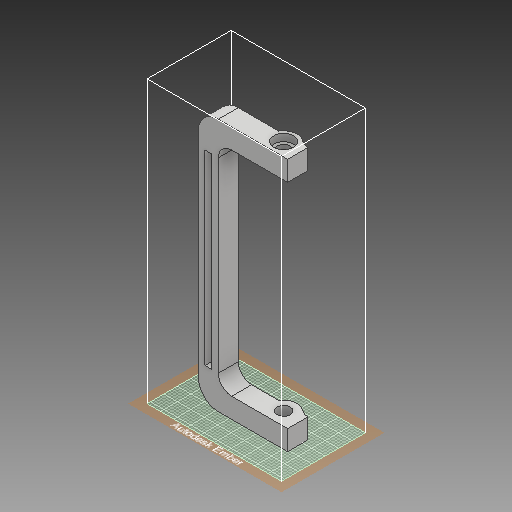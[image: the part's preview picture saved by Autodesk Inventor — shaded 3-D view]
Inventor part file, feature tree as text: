
AUTODESK INVENTOR PART (.ipt)
format: ipt  version: 2018 (Build 220112000, 112)  size: 412,160 bytes
history: native  units: in
note: dims shown in document units (in); Inventor stores cm internally (conversion verified against a paired STEP export)
features: sketch x21, extrude x14, fillet x6, hole x2, plane x1, mirror x1
ambient origin geometry x8: Origin, YZ Plane, XZ Plane, XY Plane, X Axis, Y Axis, Z Axis, Center Point
bodies: Solid1 (feature_tree)
feature tree (45):
  extrude  "Extrusion1"  Depth=0.375in
  sketch  "Sketch2"  dims[d3=0.375in d4=0.5in d5=0.375in d6=0.0in]
  extrude  "Extrusion2"  Depth=0.375in
  fillet  "Fillet1"  Radius=0.375in
  extrude  "Extrusion3"  Depth=0.375in
  extrude  "Extrusion4"  Depth=0.25in
  plane  "Work Plane1"
  mirror  "Mirror1"
  fillet  "Fillet2"  Radius=0.24in
  extrude  "Extrusion5"  Depth=0.375in
  sketch  "Sketch6"  dims[d17=1.0in d18=0.0in d19=0.24in d20=0.0in]
  extrude  "Extrusion6"  Depth=0.24in TaperAngle=0.0deg
  extrude  "Extrusion7"  Depth=0.375in
  fillet  "Fillet3"  Radius=0.25in
  fillet  "Fillet4"  Radius=0.375in
  fillet  "Fillet5"  Radius=0.25in
  fillet  "Fillet6"  Radius=0.125in
  sketch  "Sketch9"  dims[d30=0.125in d31=0.125in]
  extrude  "Extrusion8"  Depth=0.035in
  sketch  "Sketch11"  dims[d35=0.2in]
  sketch  "Sketch12"  dims[d36=0.2in d37=0.75in d38=0.375in d39=0.25in d40=0.5635in d41=0.35in d42=0.0in]
  hole  "Hole1"  [1 undecoded]
  hole  "Hole2"  [1 undecoded]
  sketch  "Sketch14"  dims[d51=3.5in d52=0.375in d53=0.0in]
  extrude  "Extrusion9"  Depth=0.375in
  extrude  "Extrusion10"  Depth=0.375in TaperAngle=0.0deg
  sketch  "Sketch17"  dims[d60=0.4375in d61=0.0in d62=0.39in]
  extrude  "Extrusion11"  Depth=0.26in
  extrude  "Extrusion12"  Depth=0.26in
  extrude  "Extrusion13"  Depth=0.39in
  extrude  "Extrusion14"  Depth=0.39in
  sketch  "Sketch1"  dims[d0=1.3in d1=0.375in]
  sketch  "Sketch3"  dims[d7=0.375in d8=0.0in d9=0.375in]
  sketch  "Sketch4"  dims[d10=0.24in d11=0.0in d12=0.25in d13=0.24in d14=0.0in]
  sketch  "Sketch5"  dims[d15=2.0in d16=0.375in]
  sketch  "Sketch7"  dims[d21=0.375in d22=0.0in d23=0.375in d24=0.25in d25=0.375in d26=0.25in d27=0.125in]
  sketch  "Sketch8"  dims[d28=0.035in d29=0.035in]
  sketch  "Sketch10"  dims[d32=4.375in d33=0.0in d34=0.2in]
  sketch  "Sketch13"  dims[d43=0.2in d44=0.75in d45=0.375in d46=0.25in d47=0.5635in d48=0.35in d49=0.0in d50=0.125in]
  sketch  "Sketch15"  dims[d54=1.0in d55=0.0in d56=0.26in]
  sketch  "Sketch16"  dims[d57=0.4375in d58=0.0in d59=0.26in]
  sketch  "Sketch18"  dims[d63=0.135in d64=0.0in d65=0.39in]
  sketch  "Sketch19"  dims[d66=0.135in d67=0.0in]
  sketch  "Sketch20"
  sketch  "Sketch21"
note: 2 required parameter values undecoded (feature->parameter linkage not recoverable at this tier; creation-order binding heuristic only, values carry confidence <= 0.55)
